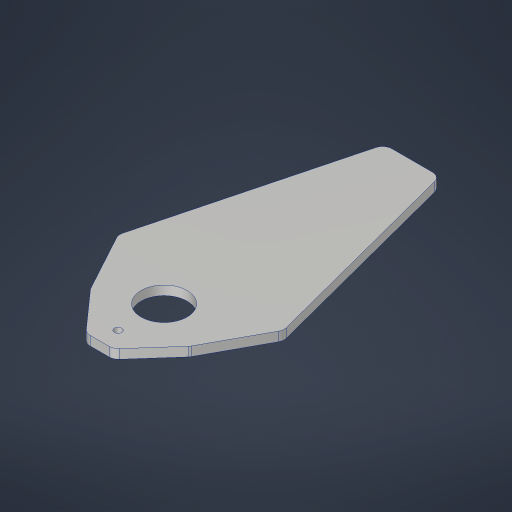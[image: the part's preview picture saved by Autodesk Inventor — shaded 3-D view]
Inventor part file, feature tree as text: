
AUTODESK INVENTOR PART (.ipt)
format: ipt  version: 2023.4 (Build 274418000, 418)  size: 215,040 bytes
history: native  units: in
note: dims shown in document units (in); Inventor stores cm internally (conversion verified against a paired STEP export)
features: fillet x3, sketch x3, hole x2, projected_geometry x2, extrude x1, chamfer x1
ambient origin geometry x8: Origin, YZ Plane, XZ Plane, XY Plane, X Axis, Y Axis, Z Axis, Center Point
bodies: Solid1 (feature_tree)
feature tree (12):
  extrude  "Extrusion1"  Depth=0.25in
  fillet  "Fillet1"  Radius=0.25in
  fillet  "Fillet2"  Radius=4.5in
  hole  "Hole1"  [1 undecoded]
  chamfer  "Chamfer1"  Distance=0.25in
  fillet  "Fillet3"  Radius=0.26in
  hole  "Hole2"  [1 undecoded]
  sketch  "Sketch1"  dims[d0=1.0in d1=2.0in d2=0.25in d3=4.5in]
  sketch  "Sketch2"  dims[d4=8.5in d5=0.75in]
  sketch  "Sketch3"  dims[d6=1.5in d7=0.25in d8=0.0in d9=0.26in d10=1.0in d11=1.25in d12=0.75in d13=0.332in d14=0.25in d15=0.5635in d16=1.0in d17=0.8108in d20=0.375in d21=1.25in d22=45.0deg d23=0.26in d24=1.25in d25=0.201in d26=0.75in d27=0.385in d28=0.25in d29=0.5635in d30=1.0in d31=0.8108in]
  projected_geometry  "Project Cut Edges1"
  projected_geometry  "Project Cut Edges2"
note: 2 required parameter values undecoded (feature->parameter linkage not recoverable at this tier; creation-order binding heuristic only, values carry confidence <= 0.55)
